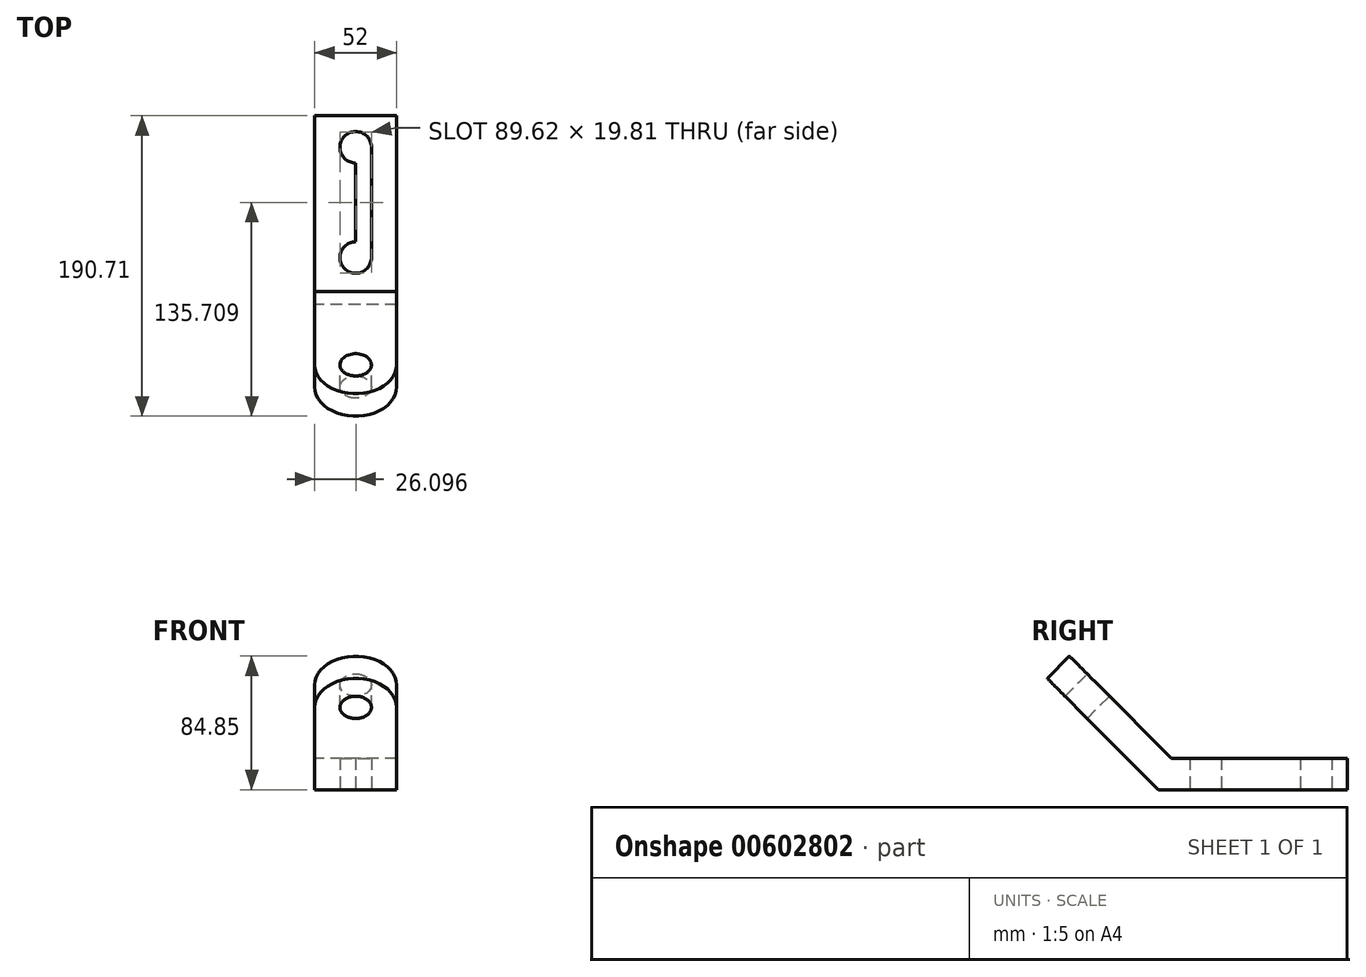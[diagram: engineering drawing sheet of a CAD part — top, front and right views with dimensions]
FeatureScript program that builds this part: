
annotation { "Feature Type Name" : "Feature", "Feature Type Description" : "" }
export const myFeature = defineFeature(function(context is Context, id is Id, definition is map)
    precondition{}
    {
        {
            var Q0;
            Q0=qCreatedBy(makeId("Right.planeOp"),FACE);
            var sketch = newSketch(context, id + "F0", { "sketchPlane" : qUnion([Q0])});
            skLineSegment(sketch, "E0.bottom", {"start": v(0, 0) * mm, "end": v(-10, 0) * mm});
            skLineSegment(sketch, "E0.top", {"start": v(0, 20) * mm, "end": v(-10, 20) * mm});
            skLineSegment(sketch, "E0.left", {"start": v(0, 0) * mm, "end": v(0, 20) * mm});
            skLineSegment(sketch, "E0.right", {"start": v(-10, 0) * mm, "end": v(-10, 20) * mm});
            skLineSegment(sketch, "E1", {"start": v(-10, 20) * mm, "end": v(-100, 20) * mm});
            skLineSegment(sketch, "E2", {"start": v(-100, 20) * mm, "end": v(-100, 0) * mm});
            skLineSegment(sketch, "E3", {"start": v(-100, 0) * mm, "end": v(-10, 0) * mm});
            skLineSegment(sketch, "E4", {"start": v(-100, 0) * mm, "end": v(-120, 0) * mm});
            skLineSegment(sketch, "E5", {"start": v(-120, 0) * mm, "end": v(-190.71, 70.71) * mm});
            skLineSegment(sketch, "E6", {"start": v(-190.71, 70.71) * mm, "end": v(-176.57, 84.85) * mm});
            skLineSegment(sketch, "E7", {"start": v(-176.57, 84.85) * mm, "end": v(-165.25, 73.54) * mm});
            skLineSegment(sketch, "E8", {"start": v(-165.25, 73.54) * mm, "end": v(-151.11, 59.4) * mm});
            skLineSegment(sketch, "E9", {"start": v(-151.11, 59.4) * mm, "end": v(-165.25, 45.25) * mm});
            skLineSegment(sketch, "E10", {"start": v(-165.25, 73.54) * mm, "end": v(-179.4, 59.4) * mm});
            skLineSegment(sketch, "E11", {"start": v(-151.11, 59.4) * mm, "end": v(-111.72, 20) * mm});
            skLineSegment(sketch, "E12", {"start": v(-100, 20) * mm, "end": v(-111.72, 20) * mm});
            skLineSegment(sketch, "E13", {"start": v(-10, 20) * mm, "end": v(-30, 20) * mm});
            skLineSegment(sketch, "E14", {"start": v(-30, 20) * mm, "end": v(-30, 0) * mm});
            skLineSegment(sketch, "E15", {"start": v(-30, 0) * mm, "end": v(-20, 0) * mm});
            skLineSegment(sketch, "E16", {"start": v(-20, 0) * mm, "end": v(-20, 20) * mm});
            skLineSegment(sketch, "E17", {"start": v(-100, 20) * mm, "end": v(-80, 20) * mm});
            skLineSegment(sketch, "E18", {"start": v(-80, 20) * mm, "end": v(-80, 0) * mm});
            skLineSegment(sketch, "E19", {"start": v(-80, 0) * mm, "end": v(-90, 0) * mm});
            skLineSegment(sketch, "E20", {"start": v(-90, 0) * mm, "end": v(-90, 20) * mm});
            skLineSegment(sketch, "E21", {"start": v(-165.25, 73.54) * mm, "end": v(-158.18, 66.47) * mm});
            skLineSegment(sketch, "E22", {"start": v(-158.18, 66.47) * mm, "end": v(-172.33, 52.33) * mm});
            skSolve(sketch);
        }
        {
            var Q0;
            Q0=qCreatedBy(makeId("Top.planeOp"),FACE);
            var sketch = newSketch(context, id + "F1", { "sketchPlane" : qUnion([Q0])});
            skLineSegment(sketch, "E23", {"start": v(0, -20) * mm, "end": v(26, -20) * mm});
            skLineSegment(sketch, "E24", {"start": v(26, -20) * mm, "end": v(26, -90) * mm});
            skLineSegment(sketch, "E25", {"start": v(26, -90) * mm, "end": v(0, -90) * mm});
            skLineSegment(sketch, "E26", {"start": v(0, -90) * mm, "end": v(0, -20) * mm});
            skLineSegment(sketch, "E27.bottom", {"start": v(26, -90) * mm, "end": v(16, -90) * mm});
            skLineSegment(sketch, "E27.top", {"start": v(26, -20) * mm, "end": v(16, -20) * mm});
            skLineSegment(sketch, "E27.left", {"start": v(26, -90) * mm, "end": v(26, -20) * mm});
            skLineSegment(sketch, "E27.right", {"start": v(16, -90) * mm, "end": v(16, -20) * mm});
            skLineSegment(sketch, "E28.bottom", {"start": v(26, -90) * mm, "end": v(36, -90) * mm});
            skLineSegment(sketch, "E28.top", {"start": v(26, -20) * mm, "end": v(36, -20) * mm});
            skLineSegment(sketch, "E28.right", {"start": v(36, -90) * mm, "end": v(36, -20) * mm});
            skLineSegment(sketch, "E29", {"start": v(0, 0) * mm, "end": v(0, -90) * mm});
            skSolve(sketch);
        }
        {
            var Q0;
            Q0 = qSketchRegion(id + "F0", true);
            extrude(context, id + "F2", {"entities" : qUnion([Q0]), "depth" : 52 * mm, "offsetDistance" : 25 * mm});
        }
        {
            var Q0;
            Q0=makeQuery(id+"F2.opExtrude","CAP_EDGE",EDGE,{"disambiguationData":[OSD([sQuery(id+"F0.wireOp",EDGE,"E6")])],"isStart":false});
            var Q1;
            Q1=makeQuery(id+"F2.opExtrude","CAP_EDGE",EDGE,{"disambiguationData":[OSD([sQuery(id+"F0.wireOp",EDGE,"E6")])],"isStart":true});
            fillet(context, id + "F3", {"entities" : qUnion([Q0, Q1]), "radius" : 26 * mm, "tangentPropagation" : true, "allowEdgeOverflow" : false});
        }
        {
            var Q0;
            Q0=sQuery(id+"F1.wireOp",VERTEX,"E25.start");
            var Q1;
            Q1=sQuery(id+"F1.wireOp",VERTEX,"E24.start");
            var Q2;
            Q2=makeQuery(id+"F2.opExtrude","SWEPT_BODY",BODY,{"disambiguationData":[OSD([sQuery(id+"F0.wireOp",EDGE,"E0.bottom"),sQuery(id+"F0.wireOp",EDGE,"E0.top"),sQuery(id+"F0.wireOp",EDGE,"E0.left"),sQuery(id+"F0.wireOp",EDGE,"E1"),sQuery(id+"F0.wireOp",EDGE,"E3"),sQuery(id+"F0.wireOp",EDGE,"E4"),sQuery(id+"F0.wireOp",EDGE,"E5"),sQuery(id+"F0.wireOp",EDGE,"E6"),sQuery(id+"F0.wireOp",EDGE,"E7"),sQuery(id+"F0.wireOp",EDGE,"E8"),sQuery(id+"F0.wireOp",EDGE,"E11"),sQuery(id+"F0.wireOp",EDGE,"E12"),sQuery(id+"F0.wireOp",EDGE,"E13"),sQuery(id+"F0.wireOp",EDGE,"E15"),sQuery(id+"F0.wireOp",EDGE,"E17"),sQuery(id+"F0.wireOp",EDGE,"E19"),sQuery(id+"F0.wireOp",EDGE,"E21")])]});
            hole(context, id + "F4", {"style" : HoleStyle.SIMPLE, "endStyle" : HoleEndStyle.THROUGH, "oppositeDirection" : true, "holeDiameter" : 20 * mm, "majorDiameter" : 5 * mm, "isTappedThrough" : true, "tappedDepth" : 12 * mm, "tapClearance" : 3, "locations" : qUnion([Q0, Q1]), "scope" : qUnion([Q2])});
        }
        {
            var Q0;
            Q0=makeQuery(id+"F1.imprint","IMPRINT",FACE,{"disambiguationData":[TD([[makeQuery(id+"F1.imprint","IMPRINT",EDGE,{"derivedFrom":sQuery(id+"F1.wireOp",EDGE,"E28.bottom")}),1.0]])]});
            var Q1;
            Q1=makeQuery(id+"F1.imprint","IMPRINT",FACE,{"disambiguationData":[TD([[makeQuery(id+"F1.imprint","IMPRINT",EDGE,{"derivedFrom":sQuery(id+"F1.wireOp",EDGE,"E27.bottom")}),-1.0]])]});
            extrude(context, id + "F5", {"entities" : qUnion([Q0, Q1]), "operationType" : NewBodyOperationType.REMOVE, "depth" : 47 * mm, "offsetDistance" : 25 * mm});
        }
        {
            var Q0;
            Q0=makeQuery(id+"F2.opExtrude","SWEPT_FACE",FACE,{"disambiguationData":[OSD([sQuery(id+"F0.wireOp",EDGE,"E7"),sQuery(id+"F0.wireOp",EDGE,"E8"),sQuery(id+"F0.wireOp",EDGE,"E11"),sQuery(id+"F0.wireOp",EDGE,"E21")])]});
            var sketch = newSketch(context, id + "F6", { "sketchPlane" : qUnion([Q0])});
            skLineSegment(sketch, "E30", {"start": v(-52, 158.85) * mm, "end": v(0, 158.85) * mm});
            skLineSegment(sketch, "E31", {"start": v(0, 158.85) * mm, "end": v(-26, 158.85) * mm});
            skSolve(sketch);
        }
        {
            var Q0;
            Q0=sQuery(id+"F6.wireOp",VERTEX,"E31.end");
            var Q1;
            Q1=makeQuery(id+"F2.opExtrude","SWEPT_BODY",BODY,{"disambiguationData":[OSD([sQuery(id+"F0.wireOp",EDGE,"E0.bottom"),sQuery(id+"F0.wireOp",EDGE,"E0.top"),sQuery(id+"F0.wireOp",EDGE,"E0.left"),sQuery(id+"F0.wireOp",EDGE,"E1"),sQuery(id+"F0.wireOp",EDGE,"E3"),sQuery(id+"F0.wireOp",EDGE,"E4"),sQuery(id+"F0.wireOp",EDGE,"E5"),sQuery(id+"F0.wireOp",EDGE,"E6"),sQuery(id+"F0.wireOp",EDGE,"E7"),sQuery(id+"F0.wireOp",EDGE,"E8"),sQuery(id+"F0.wireOp",EDGE,"E11"),sQuery(id+"F0.wireOp",EDGE,"E12"),sQuery(id+"F0.wireOp",EDGE,"E13"),sQuery(id+"F0.wireOp",EDGE,"E15"),sQuery(id+"F0.wireOp",EDGE,"E17"),sQuery(id+"F0.wireOp",EDGE,"E19"),sQuery(id+"F0.wireOp",EDGE,"E21")])]});
            hole(context, id + "F7", {"style" : HoleStyle.SIMPLE, "endStyle" : HoleEndStyle.THROUGH, "holeDiameter" : 20 * mm, "majorDiameter" : 5 * mm, "isTappedThrough" : true, "tappedDepth" : 12 * mm, "tapClearance" : 3, "locations" : qUnion([Q0]), "scope" : qUnion([Q1])});
        }
    });
